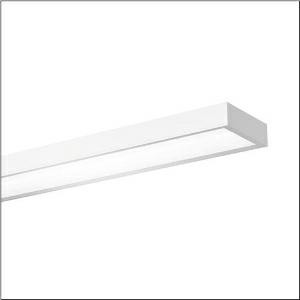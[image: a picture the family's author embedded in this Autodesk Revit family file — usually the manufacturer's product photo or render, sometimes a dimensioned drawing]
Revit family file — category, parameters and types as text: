
# Revit family: sport_31_51hs12dc4dca
name_source: partatom
category: Lighting Fixtures
units: mm (PartAtom-declared; Revit-internal decimal feet)

## family parameters
Cut with Voids When Loaded = No
Host = Face
Light Source = No
Part Type = Normal
Room Calculation Point = No
Round Connector Dimension = Use Diameter
Shared = No

## types (1)
- --- (1 x LED, 8000 lm, 59.4 W, 4000K)
    Apparent Load = 59 VA
    CIE Flux Codes = 65 89 97 100 100
    Color Rendering = 80
    Color Temperature = 4000K
    Default Elevation = 1800 mm
    Description = Sport 31, high bay luminaire, primary light control with reflector, of sheet steel, primary anti-glare with prismatic structure, of PC, primary optical cover: cover panel, of PC, light emission: direct distribution, primary light characteristic: symmetric, installation type: suspended mounting, recessed, surface-mounted, LED, rated luminous flux: 8.000lm, luminous efficacy: 135lm/W, light colour: 840, colour temperature: 4000K, control gear: DALI 2, with terminal, 5-pole, max. 2.5mm², mains connection: 220..240V, AC/DC, 50/60Hz, rated input power: 58W, housing, of sheet steel, traffic white (RAL 9016), length: 1.540mm, width: 315mm, height: 95mm, protection rating (complete): IP20, protection rating (lamp compartment, on room side): IP50, insulation class (complete): insulation class I (protective earthing), certification: CE, ENEC, UKCA, ball protection: ball impact resistant with ceiling mounting or chain suspension, impact resistance: IK08, permissible operating ambient temperature: -20..+35°C, standard: DIN 18032-3, EN 60598-2-22, packaging unit: 1 piece
    Height = 100 mm  [stored 0.328084 ft]
    Lamp = 1 x LED
    Lamp Light Flux = 8000 lm
    Lamp Power = 59.4 W
    Lamp count = 1
    Length = 1500 mm
    Luminous efficacy = 135 lm/W
    Manufacturer = Siteco
    ModVariant = No
    Model = 51HS12DC4DCA
    Mounting Place = Ceiling
    Mounting Type = Pendant
    Number of Poles = 1
    OnlyDefault = Yes
    Power Factor = 1
    Product Name = Sport 31
    Product group = high bay luminaire
    ProductGroupID = 902
    Protection Class = Protection class I
    Protection Degree = IP 20
    RLX_Detail_Level = 1
    RLX_Emergency_Light_Flux = 0 lm
    RLX_Emergency_Type = 0
    RLX_Emergency_Type_DB = No
    RlxData = <blob elided: 22757 chars, md5=fde15971>
    Socket = socket
    Standby Power = 0 W
    System Light Flux = 8000 lm
    System Power = 59 W
    Type Comments = factory setting: luminous flux: 100 % | dim-lin: 254 | 247 mA
    Type Image = l_1397489.jpg
    URL = http://relux.com
    VarID = @adj_194693
    Voltage = 0 V
    Weight = 0.00 kg
    Width = 315 mm

note: [stored X ft] marks values corroborated as IEEE doubles in the binary element streams (Revit-internal decimal feet)

## geometry (parser evidence)
native form markers: Blend x4, Sweep x10
no freeform markers — native parametric forms only
